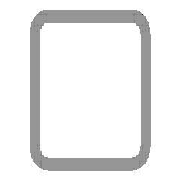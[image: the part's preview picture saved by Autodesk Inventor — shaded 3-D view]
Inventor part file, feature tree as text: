
AUTODESK INVENTOR PART (.ipt)
format: ipt  version: 2025.1 (Build 291241020, 241B)  size: 134,656 bytes
history: native  units: mm (DEFAULTED — no unit token found)
features: other x4, sketch x1, plane x1
ambient origin geometry x8: Origin, YZ Plane, XZ Plane, XY Plane, X Axis, Y Axis, Z Axis, Center Point
bodies: Solid1 (feature_tree), Body (feature_tree)
feature tree (6):
  parser-record x1  (decoder bookkeeping rows leaked as tree rows — omitted from the tree; the rows remain in map.json)
  other  "Driven Length"
  other  "Start Plane"
  other  "End Plane"
  sketch  "Sketch3"  dims[d3=520.0mm d4=0.0mm d7=4.0mm d9=40.0mm d11=40.0mm d12=2.0mm d13=40.0mm d14=560.0mm d15=20.0mm d16=20.0mm d17=90.0deg d18=520.0mm]
  plane  "Work Plane3"
